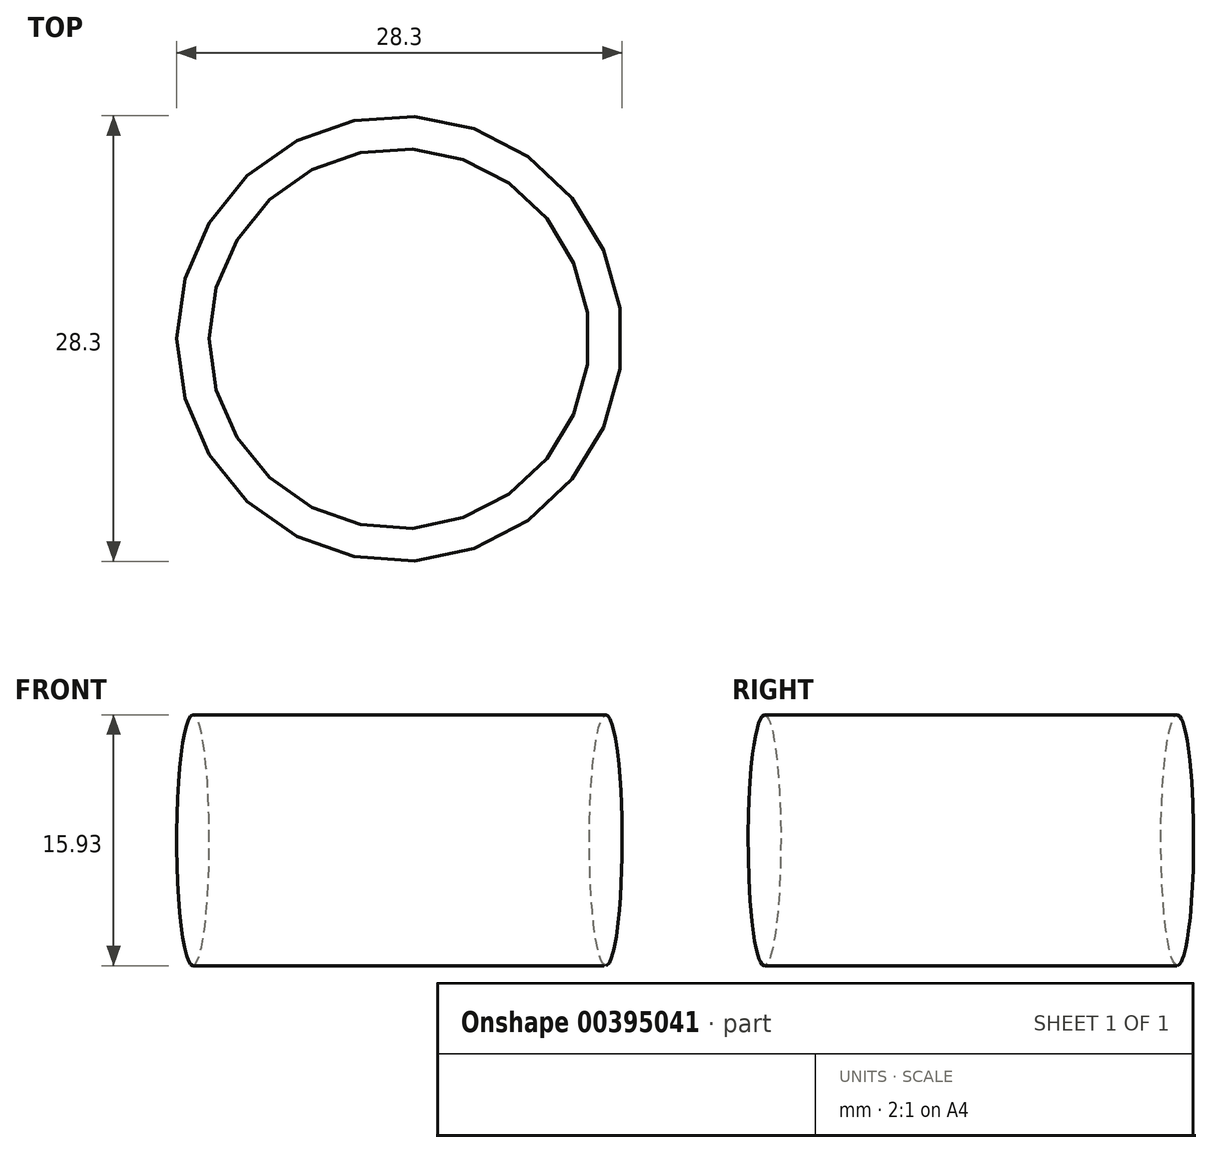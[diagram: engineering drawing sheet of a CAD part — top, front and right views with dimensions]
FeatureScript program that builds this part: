
annotation { "Feature Type Name" : "Feature", "Feature Type Description" : "" }
export const myFeature = defineFeature(function(context is Context, id is Id, definition is map)
    precondition{}
    {
        {
            var Q0;
            Q0=qCreatedBy(makeId("Front.planeOp"),FACE);
            var sketch = newSketch(context, id + "F0", { "sketchPlane" : qUnion([Q0])});
            skLineSegment(sketch, "E0", {"start": v(0, 0) * mm, "end": v(13.11, 0) * mm});
            skLineSegment(sketch, "E1", {"start": v(13.11, 0) * mm, "end": v(13.11, 15.93) * mm});
            skEllipse(sketch, "E2", {"center": v(0, 7.96) * mm, "majorRadius": 7.96 * mm, "minorRadius": 1.04 * mm, "majorAxis": v(0, -1)});
            skPoint(sketch, "E2.centerSnap0", {"position": v(13.11, 7.96) * mm});
            skSolve(sketch);
        }
        {
            var Q0;
            Q0=makeQuery(id+"F0.imprint","IMPRINT",FACE,{"disambiguationData":[TD([[makeQuery(id+"F0.imprint","IMPRINT",EDGE,{"derivedFrom":sQuery(id+"F0.wireOp",EDGE,"E2")}),1.0]])]});
            var Q1;
            Q1=sQuery(id+"F0.wireOp",EDGE,"E1");
            revolve(context, id + "F1", {"entities" : qUnion([Q0]), "axis" : qUnion([Q1]), "revolveType" : RevolveType.FULL});
        }
    });
